# Revit family: IS_StradaII_T2991_BIM_FR
name_source: partatom
category: Plumbing Fixtures
revit_build: Autodesk Revit 2017 (Build: 20160225_1515(x64)
units: mm (PartAtom-declared; Revit-internal decimal feet)

## family parameters
Always vertical = No
Cut with Voids When Loaded = No
OmniClass Number = 23.45.05.14.14
OmniClass Title = Sinks/Lavatories
Part Type = Normal
Room Calculation Point = No
Round Connector Dimension = Use Diameter
Shared = No
Work Plane-Based = No

## types (2) — shared parameters
Accessoires = www.idealstandard.be
Auteur = Ideal Standard
BOSUseNativeGeometries = 1
Bim-NomDuProjet = ISI_IdealStandard_
Caractéristiques = STRADA II VTY LAVABO 60 WHT IP 1TH
CodeBarre = 8014140450467
ConseilsDInstallation = www.idealstandard.be
Couleur = Blanc
DateDeCréation = 2018_08_15
Description = STRADA II VTY LAVABO 60 WHT IP 1TH
DiamètreÉvacuation = 31.8
Dimensions = 188 x 640 x 462mm
Espace = Interne
Finition = Blanc
Forme = Complexe
Hauteur = 188 mm
IfcExportAs = IfcSanitaryTerminalType
IfcExportType = WASHHANDBASIN
InformationsProduit = www.idealstandard.be
Largeur = 640 mm  [stored 2.09974 ft]
LienUtile = www.idealstandard.be
Longueur = 462 mm
Manufacturer = www.idealstandard.be
Marque = Ideal Standard
Montage/PoseDuLavabo = Pedestal Wash basins
Raccordement = Plomberie
Révision = 1
TypeDeLavabo = Lavabos sur piédestal
URL = www.idealstandard.be
Uniclass2015Code = Pr_40_20_96_63
Uniclass2015Title = Pedestal Wash basins
Uniclass2015Version = Products v1.1
UnitéDeMesure = Millimètres
UnitéDeTemps = An
UnitéMonétaire = €
UrlDuFabricant = www.idealstandard.be
Version = 1
zero-valued in all types: Cost, CoûtDeRemplacement, Profondeur

## per-type parameters (varying)
| type | Model | PoidsNet |
| T299101 - STRADA II VTY BSN 60 WHITE 1TH | T299101 | 17,20 KG |
| T2991MA - STRADA II VTY BSN 60 WHT IP 1TH | T2991MA | 7,20 KG |

note: [stored X ft] marks values corroborated as IEEE doubles in the binary element streams (Revit-internal decimal feet)

## geometry (parser evidence)
native form markers: Sweep x3
no freeform markers — native parametric forms only
